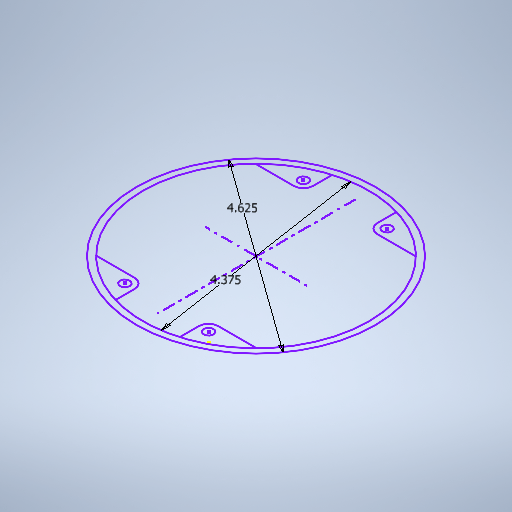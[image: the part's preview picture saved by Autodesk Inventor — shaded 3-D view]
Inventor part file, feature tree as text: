
AUTODESK INVENTOR PART (.ipt)
format: ipt  version: 2025.1 (Build 291241000, 241)  size: 245,760 bytes
history: native  units: in
note: dims shown in document units (in); Inventor stores cm internally (conversion verified against a paired STEP export)
features: sketch x1
ambient origin geometry x8: Origin, YZ Plane, XZ Plane, XY Plane, X Axis, Y Axis, Z Axis, Center Point
feature tree (1):
  sketch  "Sketch1"  dims[d3=4.375in d4=4.625in]
